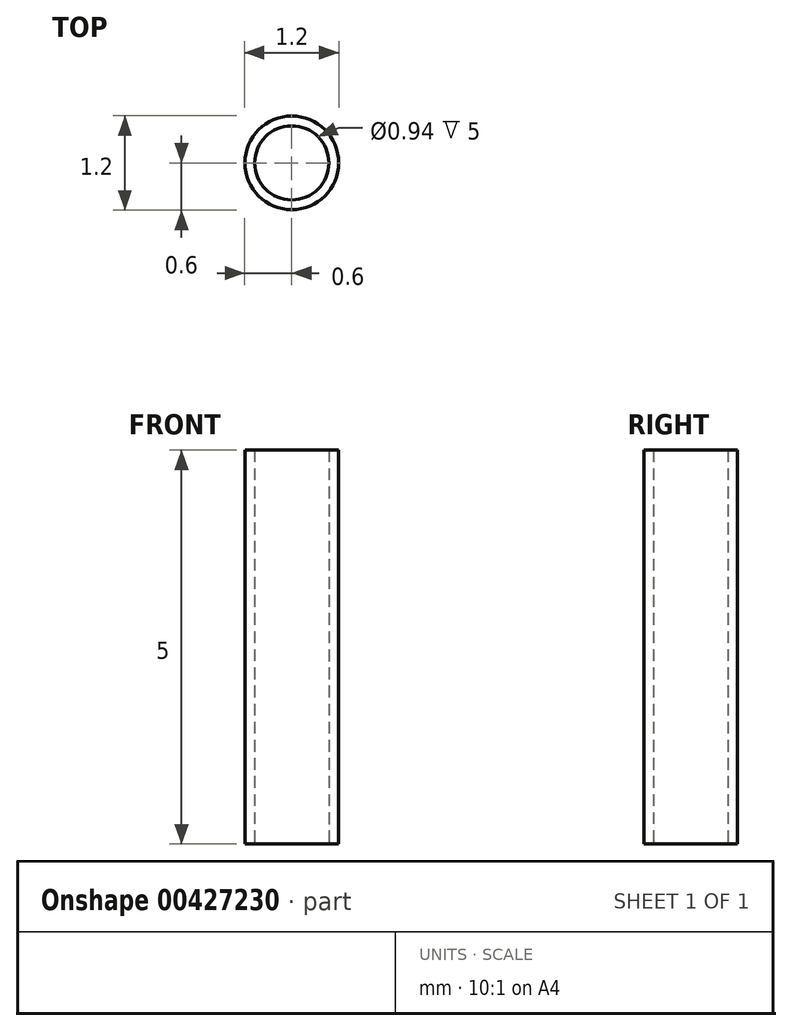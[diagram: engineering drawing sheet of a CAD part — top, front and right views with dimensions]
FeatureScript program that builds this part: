
annotation { "Feature Type Name" : "Feature", "Feature Type Description" : "" }
export const myFeature = defineFeature(function(context is Context, id is Id, definition is map)
    precondition{}
    {
        {
            var Q0;
            Q0=qCreatedBy(makeId("Top.planeOp"),FACE);
            var sketch = newSketch(context, id + "F0", { "sketchPlane" : qUnion([Q0])});
            skCircle(sketch, "E0", {"center": v(0, 0) * mm, "radius": 0.6 * mm});
            skCircle(sketch, "E1", {"center": v(0, 0) * mm, "radius": 0.47 * mm});
            skSolve(sketch);
        }
        {
            var Q0;
            Q0=makeQuery(id+"F0.imprint","IMPRINT",FACE,{"disambiguationData":[TD([[makeQuery(id+"F0.imprint","IMPRINT",EDGE,{"derivedFrom":sQuery(id+"F0.wireOp",EDGE,"E0")}),1.0]])]});
            extrude(context, id + "F1", {"entities" : qUnion([Q0]), "depth" : 5 * mm});
        }
    });
